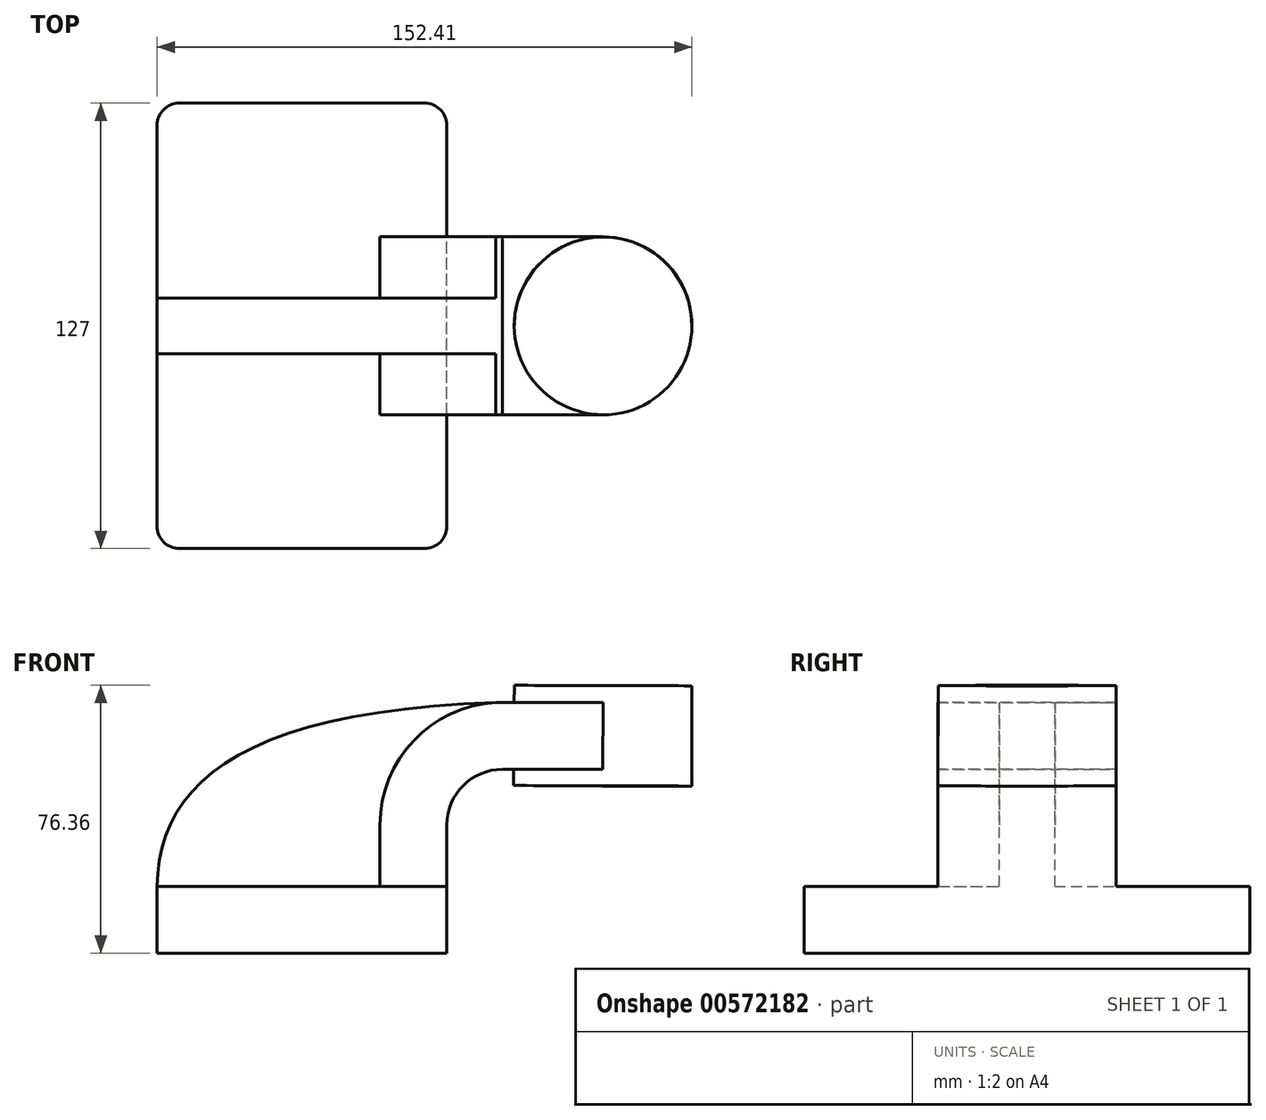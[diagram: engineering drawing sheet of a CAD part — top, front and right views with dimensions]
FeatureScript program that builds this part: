
annotation { "Feature Type Name" : "Feature", "Feature Type Description" : "" }
export const myFeature = defineFeature(function(context is Context, id is Id, definition is map)
    precondition{}
    {
        {
            var Q0;
            Q0=qCreatedBy(makeId("Front.planeOp"),FACE);
            var sketch = newSketch(context, id + "F0", { "sketchPlane" : qUnion([Q0])});
            skLineSegment(sketch, "E0.bottom", {"start": v(-41.28, -9.53) * mm, "end": v(41.28, -9.53) * mm});
            skLineSegment(sketch, "E0.top", {"start": v(-41.28, 9.53) * mm, "end": v(41.28, 9.53) * mm});
            skLineSegment(sketch, "E0.left", {"start": v(-41.28, -9.53) * mm, "end": v(-41.28, 9.53) * mm});
            skLineSegment(sketch, "E0.right", {"start": v(41.28, -9.53) * mm, "end": v(41.28, 9.52) * mm});
            skPoint(sketch, "E0.middle", {"position": v(0, 0) * mm});
            skLineSegment(sketch, "E1.bottom", {"start": v(111.12, 38.1) * mm, "end": v(60.32, 38.1) * mm});
            skLineSegment(sketch, "E1.top", {"start": v(111.12, 66.68) * mm, "end": v(60.32, 66.68) * mm});
            skLineSegment(sketch, "E1.left", {"start": v(111.12, 38.1) * mm, "end": v(111.12, 66.68) * mm});
            skLineSegment(sketch, "E1.right", {"start": v(60.32, 38.1) * mm, "end": v(60.32, 66.68) * mm});
            skPoint(sketch, "E1.middle", {"position": v(85.72, 52.39) * mm});
            skLineSegment(sketch, "E2", {"start": v(41.28, 9.52) * mm, "end": v(41.28, 27) * mm});
            skArc(sketch, "E3", {"start": v(41.27, 27) * mm, "mid": v(45.92, 38.23) * mm, "end": v(57.15, 42.88) * mm});
            skLineSegment(sketch, "E4", {"start": v(57.15, 42.88) * mm, "end": v(85.81, 42.88) * mm});
            skLineSegment(sketch, "E5.0", {"start": v(57.15, 61.93) * mm, "end": v(85.81, 61.93) * mm});
            skArc(sketch, "E5.1", {"start": v(22.23, 27) * mm, "mid": v(32.45, 51.7) * mm, "end": v(57.15, 61.93) * mm});
            skLineSegment(sketch, "E5.2", {"start": v(22.23, 9.52) * mm, "end": v(22.23, 27) * mm});
            skLineSegment(sketch, "E6", {"start": v(85.72, 38.1) * mm, "end": v(85.81, 66.68) * mm});
            skFitSpline(sketch, "E7", {"points": [v(-41.28, 9.53) * mm, v(57.15, 61.93) * mm], "startDerivative": vector(0.5, 87.4) * mm, "endDerivative": vector(221.97, 5.56) * mm});
            skSolve(sketch);
        }
        {
            var Q0;
            Q0=makeQuery(id+"F0.imprint","IMPRINT",FACE,{"disambiguationData":[TD([[makeQuery(id+"F0.imprint","IMPRINT",EDGE,{"derivedFrom":sQuery(id+"F0.wireOp",EDGE,"E0.bottom")}),1.0]])]});
            extrude(context, id + "F1", {"entities" : qUnion([Q0]), "endBound" : BoundingType.SYMMETRIC, "depth" : 127 * mm, "offsetDistance" : 25.4 * mm});
        }
        {
            var Q0;
            {var subQ1=sQuery(id+"F0.wireOp",EDGE,"E2");Q0=makeQuery(id+"F0.imprint","IMPRINT",FACE,{"disambiguationData":[TD([[makeQuery(id+"F0.imprint","IMPRINT",EDGE,{"derivedFrom":subQ1}),1.0]])]});}
            var Q1;
            {var subQ0=sQuery(id+"F0.wireOp",EDGE,"E4");var subQ1=sQuery(id+"F0.wireOp",EDGE,"E1.right");var subQ2=makeQuery(id+"F0.imprint","INTERSECT",VERTEX,{"derivedFrom":[subQ1,subQ0]});Q1=makeQuery(id+"F0.imprint","IMPRINT",FACE,{"disambiguationData":[TD([[makeQuery(id+"F0.imprint","IMPRINT",EDGE,{"disambiguationData":[TD([[subQ2,-1.0]])],"derivedFrom":subQ1}),-1.0]])]});}
            extrude(context, id + "F2", {"entities" : qUnion([Q0, Q1]), "operationType" : NewBodyOperationType.ADD, "endBound" : BoundingType.SYMMETRIC, "depth" : 50.8 * mm, "offsetDistance" : 25.4 * mm});
        }
        {
            var Q0;
            {var subQ3=sQuery(id+"F0.wireOp",EDGE,"E5.2");Q0=makeQuery(id+"F0.imprint","IMPRINT",FACE,{"disambiguationData":[TD([[makeQuery(id+"F0.imprint","IMPRINT",EDGE,{"derivedFrom":subQ3}),1.0]])]});}
            extrude(context, id + "F3", {"entities" : qUnion([Q0]), "operationType" : NewBodyOperationType.ADD, "endBound" : BoundingType.SYMMETRIC, "depth" : 15.88 * mm, "offsetDistance" : 25.4 * mm});
        }
        {
            var Q0;
            {var subQ0=sQuery(id+"F0.wireOp",EDGE,"E1.left");Q0=makeQuery(id+"F0.imprint","IMPRINT",FACE,{"disambiguationData":[TD([[makeQuery(id+"F0.imprint","IMPRINT",EDGE,{"derivedFrom":subQ0}),1.0]])]});}
            var Q1;
            Q1=sQuery(id+"F0.wireOp",EDGE,"E6");
            var Q2;
            Q2=sQuery(id+"F0.wireOp",EDGE,"E6");
            revolve(context, id + "F4", {"operationType" : NewBodyOperationType.ADD, "entities" : qUnion([Q0]), "surfaceEntities" : qUnion([Q1]), "axis" : qUnion([Q2]), "revolveType" : RevolveType.FULL});
        }
        {
            var Q0;
            Q0=makeQuery(id+"F1.opExtrude","CAP_EDGE",EDGE,{"disambiguationData":[OSD([sQuery(id+"F0.wireOp",EDGE,"E0.right")])],"isStart":false});
            var Q1;
            Q1=makeQuery(id+"F1.opExtrude","CAP_EDGE",EDGE,{"disambiguationData":[OSD([sQuery(id+"F0.wireOp",EDGE,"E0.left")])],"isStart":false});
            var Q2;
            Q2=makeQuery(id+"F1.opExtrude","CAP_EDGE",EDGE,{"disambiguationData":[OSD([sQuery(id+"F0.wireOp",EDGE,"E0.right")])],"isStart":true});
            var Q3;
            Q3=makeQuery(id+"F1.opExtrude","CAP_EDGE",EDGE,{"disambiguationData":[OSD([sQuery(id+"F0.wireOp",EDGE,"E0.left")])],"isStart":true});
            fillet(context, id + "F5", {"entities" : qUnion([Q0, Q1, Q2, Q3]), "radius" : 6.35 * mm, "tangentPropagation" : true, "allowEdgeOverflow" : false});
        }
    });
